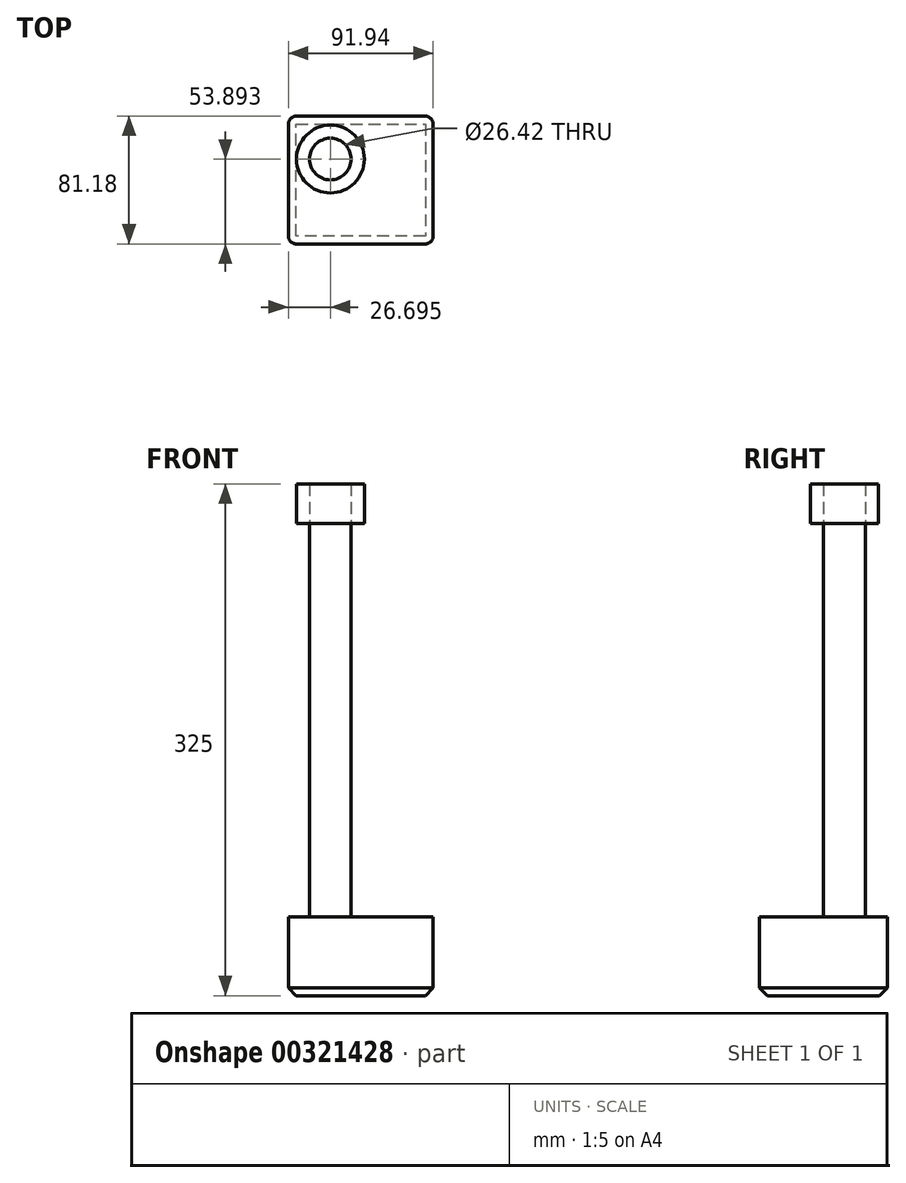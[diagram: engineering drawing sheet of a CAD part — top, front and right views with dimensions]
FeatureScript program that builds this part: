
annotation { "Feature Type Name" : "Feature", "Feature Type Description" : "" }
export const myFeature = defineFeature(function(context is Context, id is Id, definition is map)
    precondition{}
    {
        {
            var Q0;
            Q0=qCreatedBy(makeId("Top.planeOp"),FACE);
            var sketch = newSketch(context, id + "F0", { "sketchPlane" : qUnion([Q0])});
            skLineSegment(sketch, "E0.bottom", {"start": v(45.97, 40.6) * mm, "end": v(-45.97, 40.6) * mm});
            skLineSegment(sketch, "E0.top", {"start": v(45.97, -40.6) * mm, "end": v(-45.97, -40.6) * mm});
            skLineSegment(sketch, "E0.left", {"start": v(45.97, 40.6) * mm, "end": v(45.97, -40.6) * mm});
            skLineSegment(sketch, "E0.right", {"start": v(-45.97, 40.6) * mm, "end": v(-45.97, -40.6) * mm});
            skPoint(sketch, "E0.middle", {"position": v(0, 0) * mm});
            skSolve(sketch);
        }
        {
            var Q0;
            Q0=makeQuery(id+"F0.imprint","IMPRINT",FACE,{"disambiguationData":[TD([[makeQuery(id+"F0.imprint","IMPRINT",EDGE,{"derivedFrom":sQuery(id+"F0.wireOp",EDGE,"E0.bottom")}),1.0]])]});
            extrude(context, id + "F1", {"entities" : qUnion([Q0]), "depth" : 50 * mm});
        }
        {
            var Q0;
            Q0=makeQuery(id+"F1.opExtrude","SWEPT_EDGE",EDGE,{"disambiguationData":[OSD([sQuery(id+"F0.wireOp",EDGE,"E0.top"),sQuery(id+"F0.wireOp",EDGE,"E0.right")])]});
            var Q1;
            Q1=makeQuery(id+"F1.opExtrude","SWEPT_EDGE",EDGE,{"disambiguationData":[OSD([sQuery(id+"F0.wireOp",EDGE,"E0.top"),sQuery(id+"F0.wireOp",EDGE,"E0.left")])]});
            var Q2;
            Q2=makeQuery(id+"F1.opExtrude","SWEPT_EDGE",EDGE,{"disambiguationData":[OSD([sQuery(id+"F0.wireOp",EDGE,"E0.bottom"),sQuery(id+"F0.wireOp",EDGE,"E0.left")])]});
            var Q3;
            Q3=makeQuery(id+"F1.opExtrude","SWEPT_EDGE",EDGE,{"disambiguationData":[OSD([sQuery(id+"F0.wireOp",EDGE,"E0.bottom"),sQuery(id+"F0.wireOp",EDGE,"E0.right")])]});
            fillet(context, id + "F2", {"entities" : qUnion([Q0, Q1, Q2, Q3]), "radius" : 5 * mm, "tangentPropagation" : true, "allowEdgeOverflow" : false});
        }
        {
            var Q0;
            Q0=makeQuery(id+"F1.opExtrude","CAP_FACE",FACE,{"disambiguationData":[OSD([sQuery(id+"F0.wireOp",EDGE,"E0.bottom"),sQuery(id+"F0.wireOp",EDGE,"E0.top"),sQuery(id+"F0.wireOp",EDGE,"E0.left"),sQuery(id+"F0.wireOp",EDGE,"E0.right")])],"isStart":false});
            var sketch = newSketch(context, id + "F3", { "sketchPlane" : qUnion([Q0])});
            skCircle(sketch, "E1", {"center": v(-19.28, 13.3) * mm, "radius": 13.21 * mm});
            skSolve(sketch);
        }
        {
            var Q0;
            Q0 = qSketchRegion(id + "F3", true);
            extrude(context, id + "F4", {"entities" : qUnion([Q0]), "operationType" : NewBodyOperationType.ADD, "depth" : 250 * mm});
        }
        {
            var Q0;
            Q0=makeQuery(id+"F1.opExtrude","CAP_EDGE",EDGE,{"disambiguationData":[OSD([sQuery(id+"F0.wireOp",EDGE,"E0.left")])],"isStart":true});
            chamfer(context, id + "F5", {"entities" : qUnion([Q0]), "width" : 5 * mm, "tangentPropagation" : true});
        }
        {
            var Q0;
            Q0=makeQuery(id+"F4.opExtrude","CAP_FACE",FACE,{"disambiguationData":[OSD([sQuery(id+"F3.wireOp",EDGE,"E1")])],"isStart":false});
            var sketch = newSketch(context, id + "F6", { "sketchPlane" : qUnion([Q0])});
            skCircle(sketch, "E2", {"center": v(-19.28, 13.3) * mm, "radius": 21.52 * mm});
            skSolve(sketch);
        }
        {
            var Q0;
            Q0=makeQuery(id+"F6.imprint","IMPRINT",FACE,{"disambiguationData":[TD([[makeQuery(id+"F6.imprint","IMPRINT",EDGE,{"derivedFrom":sQuery(id+"F6.wireOp",EDGE,"E2")}),1.0]])]});
            extrude(context, id + "F7", {"entities" : qUnion([Q0]), "depth" : 25 * mm});
        }
    });
